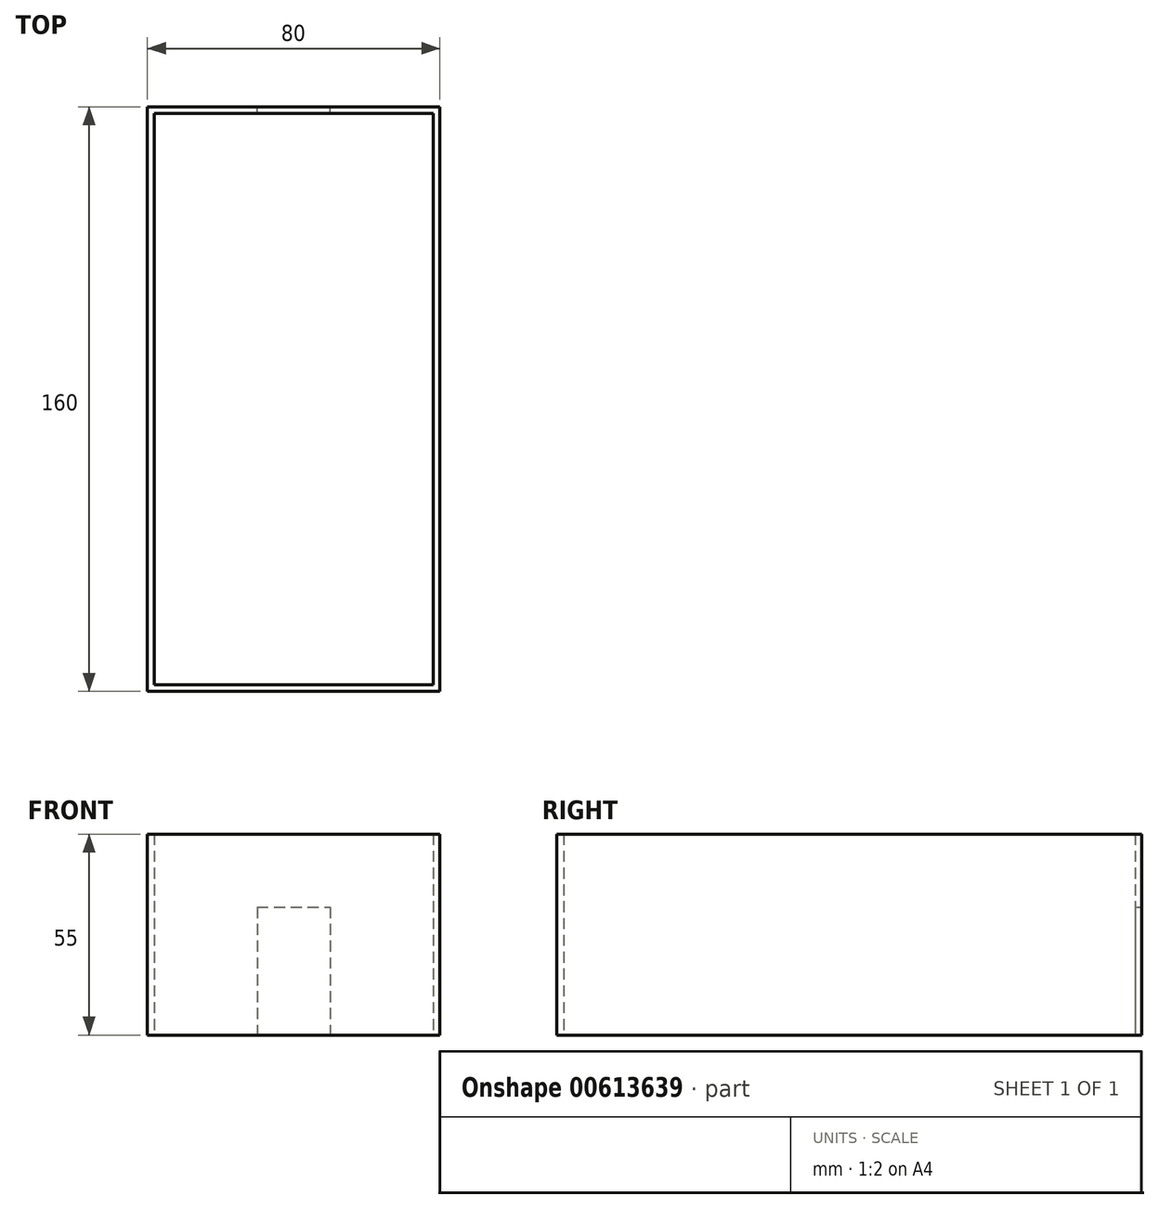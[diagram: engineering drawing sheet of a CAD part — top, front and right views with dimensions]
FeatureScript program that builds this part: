
annotation { "Feature Type Name" : "Feature", "Feature Type Description" : "" }
export const myFeature = defineFeature(function(context is Context, id is Id, definition is map)
    precondition{}
    {
        {
            var Q0;
            Q0=qCreatedBy(makeId("Front.planeOp"),FACE);
            var sketch = newSketch(context, id + "F0", { "sketchPlane" : qUnion([Q0])});
            skLineSegment(sketch, "E0.top", {"start": v(-40, -40) * mm, "end": v(40, -40) * mm});
            skLineSegment(sketch, "E0.left", {"start": v(-40, 15) * mm, "end": v(-40, -40) * mm});
            skLineSegment(sketch, "E0.right", {"start": v(40, 15) * mm, "end": v(40, -40) * mm});
            skPoint(sketch, "E0.middle", {"position": v(0, 0) * mm});
            skLineSegment(sketch, "E1", {"start": v(0, 0) * mm, "end": v(0, -5) * mm});
            skLineSegment(sketch, "E2.bottom", {"start": v(-10, -40) * mm, "end": v(10, -40) * mm});
            skLineSegment(sketch, "E2.left", {"start": v(-10, -40) * mm, "end": v(-10, -5) * mm});
            skLineSegment(sketch, "E2.right", {"start": v(10, -40) * mm, "end": v(10, -5) * mm});
            skPoint(sketch, "E2.middle", {"position": v(0, -5) * mm});
            skLineSegment(sketch, "E3", {"start": v(10, -5) * mm, "end": v(0, -5) * mm});
            skPoint(sketch, "E2.top.start.orphan", {"position": v(-10, 30) * mm});
            skPoint(sketch, "E4.orphan", {"position": v(10, 30) * mm});
            skPoint(sketch, "E5.orphan", {"position": v(0, -40) * mm});
            skLineSegment(sketch, "E6", {"start": v(-40, 0) * mm, "end": v(-40, 15) * mm});
            skLineSegment(sketch, "E7", {"start": v(-40, 15) * mm, "end": v(40, 15) * mm});
            skPoint(sketch, "E0.bottom.end.orphan", {"position": v(40, 40) * mm});
            skPoint(sketch, "E8.orphan", {"position": v(-40, 40) * mm});
            skSolve(sketch);
        }
        {
            var Q0;
            {var subQ6=sQuery(id+"F0.wireOp",EDGE,"E0.right");Q0=makeQuery(id+"F0.imprint","IMPRINT",FACE,{"disambiguationData":[TD([[makeQuery(id+"F0.imprint","IMPRINT",EDGE,{"derivedFrom":subQ6}),-1.0]])]});}
            extrude(context, id + "F1", {"entities" : qUnion([Q0]), "depth" : 160 * mm, "offsetDistance" : 25 * mm});
        }
        {
            var Q0;
            Q0=qCreatedBy(makeId("Front.planeOp"),FACE);
            var sketch = newSketch(context, id + "F2", { "sketchPlane" : qUnion([Q0])});
            skLineSegment(sketch, "E9", {"start": v(0, 0) * mm, "end": v(0, -5) * mm});
            skLineSegment(sketch, "E10", {"start": v(0, -5) * mm, "end": v(10, -5) * mm});
            skLineSegment(sketch, "E11.bottom", {"start": v(10, -5) * mm, "end": v(-10, -5) * mm});
            skLineSegment(sketch, "E11.top", {"start": v(10, -40) * mm, "end": v(-10, -40) * mm});
            skLineSegment(sketch, "E11.left", {"start": v(10, -5) * mm, "end": v(10, -40) * mm});
            skLineSegment(sketch, "E11.right", {"start": v(-10, -5) * mm, "end": v(-10, -40) * mm});
            skSolve(sketch);
        }
        {
            var Q0;
            Q0=makeQuery(id+"F1.opExtrude","SWEPT_FACE",FACE,{"disambiguationData":[OSD([sQuery(id+"F0.wireOp",EDGE,"E7")])]});
            var Q1;
            Q1=makeQuery(id+"F1.opExtrude","SWEPT_FACE",FACE,{"disambiguationData":[OSD([sQuery(id+"F0.wireOp",EDGE,"E0.top")])]});
            shell(context, id + "F3", {"entities" : qUnion([Q0, Q1]), "thickness" : 1.8 * mm});
        }
        {
            var Q0;
            Q0=makeQuery(id+"F2.imprint","IMPRINT",FACE,{"disambiguationData":[TD([[makeQuery(id+"F2.imprint","IMPRINT",EDGE,{"derivedFrom":sQuery(id+"F2.wireOp",EDGE,"E10")}),-1.0]])]});
            extrude(context, id + "F4", {"entities" : qUnion([Q0]), "operationType" : NewBodyOperationType.REMOVE, "depth" : 1.8 * mm, "offsetDistance" : 25 * mm});
        }
    });
